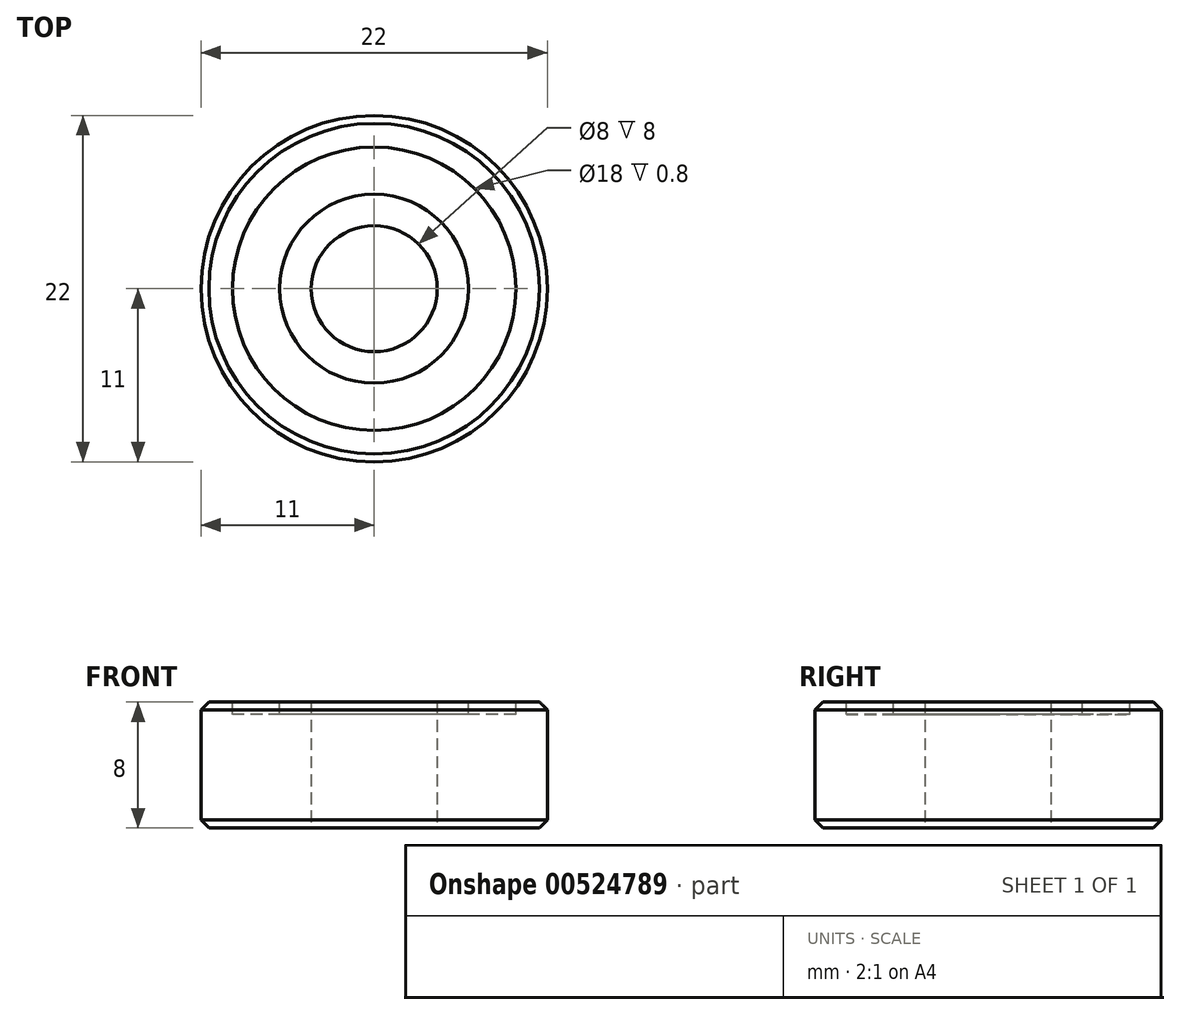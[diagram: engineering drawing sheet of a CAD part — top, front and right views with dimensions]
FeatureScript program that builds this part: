
annotation { "Feature Type Name" : "Feature", "Feature Type Description" : "" }
export const myFeature = defineFeature(function(context is Context, id is Id, definition is map)
    precondition{}
    {
        {
            var Q0;
            Q0=qCreatedBy(makeId("Top.planeOp"),FACE);
            var sketch = newSketch(context, id + "F0", { "sketchPlane" : qUnion([Q0])});
            skCircle(sketch, "E0", {"center": v(0, 0) * mm, "radius": 11 * mm});
            skCircle(sketch, "E1", {"center": v(0, 0) * mm, "radius": 4 * mm});
            skSolve(sketch);
        }
        {
            var Q0;
            Q0=qSketchRegion(id+"F0",true);
            extrude(context, id + "F1", {"entities" : qUnion([Q0]), "endBound" : BoundingType.SYMMETRIC, "depth" : 8 * mm, "offsetDistance" : 25 * mm});
        }
        {
            var Q0;
            Q0=makeQuery(id+"F1.opExtrude","CAP_FACE",FACE,{"disambiguationData":[OSD([sQuery(id+"F0.wireOp",EDGE,"E0"),sQuery(id+"F0.wireOp",EDGE,"E1")])],"isStart":false});
            var sketch = newSketch(context, id + "F2", { "sketchPlane" : qUnion([Q0])});
            skCircle(sketch, "E2.0", {"center": v(0, 0) * mm, "radius": 6 * mm});
            skCircle(sketch, "E3.0", {"center": v(0, 0) * mm, "radius": 9 * mm});
            skSolve(sketch);
        }
        {
            var Q0;
            Q0=makeQuery(id+"F2.imprint","IMPRINT",FACE,{"disambiguationData":[TD([[makeQuery(id+"F2.imprint","IMPRINT",EDGE,{"derivedFrom":sQuery(id+"F2.wireOp",EDGE,"E2.0")}),-1.0]])]});
            extrude(context, id + "F3", {"entities" : qUnion([Q0]), "operationType" : NewBodyOperationType.REMOVE, "oppositeDirection" : true, "depth" : .8 * mm, "offsetDistance" : 25 * mm});
        }
        {
            var Q0;
            Q0=makeQuery(id+"F1.opExtrude","CAP_EDGE",EDGE,{"disambiguationData":[OSD([sQuery(id+"F0.wireOp",EDGE,"E0")])],"isStart":false});
            var Q1;
            Q1=makeQuery(id+"F1.opExtrude","CAP_EDGE",EDGE,{"disambiguationData":[OSD([sQuery(id+"F0.wireOp",EDGE,"E0")])],"isStart":true});
            chamfer(context, id + "F4", {"entities" : qUnion([Q0, Q1]), "width" : .5 * mm, "tangentPropagation" : true});
        }
    });
